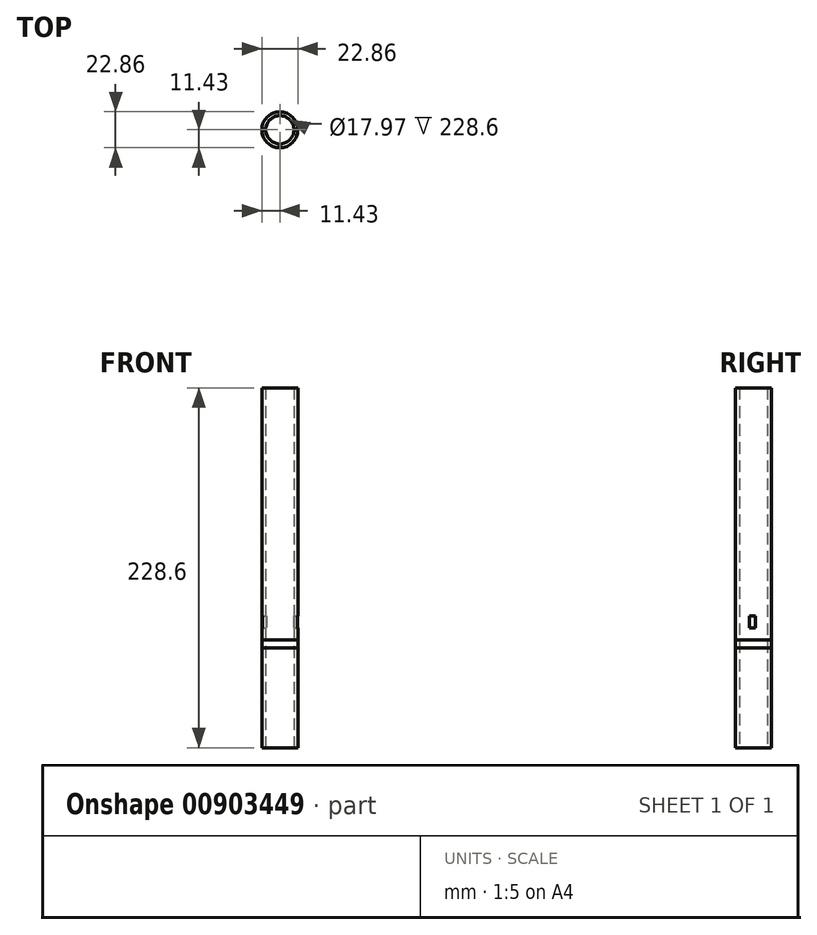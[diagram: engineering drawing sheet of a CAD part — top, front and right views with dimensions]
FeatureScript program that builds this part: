
annotation { "Feature Type Name" : "Feature", "Feature Type Description" : "" }
export const myFeature = defineFeature(function(context is Context, id is Id, definition is map)
    precondition{}
    {
        {
            var Q0;
            Q0=qCreatedBy(makeId("Top.planeOp"),FACE);
            var sketch = newSketch(context, id + "F0", { "sketchPlane" : qUnion([Q0])});
            skCircle(sketch, "E0", {"center": v(0, 0) * mm, "radius": 8.99 * mm});
            skCircle(sketch, "E1", {"center": v(0, 0) * mm, "radius": 11.43 * mm});
            skSolve(sketch);
        }
        {
            var Q0;
            Q0=makeQuery(id+"F0.imprint","IMPRINT",FACE,{"disambiguationData":[TD([[makeQuery(id+"F0.imprint","IMPRINT",EDGE,{"derivedFrom":sQuery(id+"F0.wireOp",EDGE,"E0")}),-1.0]])]});
            extrude(context, id + "F1", {"entities" : qUnion([Q0]), "depth" : 228.6 * mm, "offsetDistance" : 25.4 * mm});
        }
        {
            var Q0;
            Q0=qCreatedBy(makeId("Top.planeOp"),FACE);
            cPlane(context, id + "F2", {"entities" : qUnion([Q0]), "cplaneType" : CPlaneType.OFFSET, "offset" : 76.2 * mm, "width" : 152.4 * mm, "height" : 152.4 * mm});
        }
        {
            var Q0;
            Q0=qCreatedBy(id+"F2.planeOp",FACE);
            var sketch = newSketch(context, id + "F3", { "sketchPlane" : qUnion([Q0])});
            skLineSegment(sketch, "E2.bottom", {"start": v(-13.95, 1.1) * mm, "end": v(14.76, 1.1) * mm});
            skLineSegment(sketch, "E2.top", {"start": v(-13.95, -2.74) * mm, "end": v(14.76, -2.74) * mm});
            skLineSegment(sketch, "E2.left", {"start": v(-13.95, 1.1) * mm, "end": v(-13.95, -2.74) * mm});
            skLineSegment(sketch, "E2.right", {"start": v(14.76, 1.1) * mm, "end": v(14.76, -2.74) * mm});
            skSolve(sketch);
        }
        {
            var Q0;
            Q0=makeQuery(id+"F3.imprint","IMPRINT",FACE,{"disambiguationData":[TD([[makeQuery(id+"F3.imprint","IMPRINT",EDGE,{"derivedFrom":sQuery(id+"F3.wireOp",EDGE,"E2.bottom")}),-1.0]])]});
            extrude(context, id + "F4", {"entities" : qUnion([Q0]), "operationType" : NewBodyOperationType.REMOVE, "depth" : 7.62 * mm, "offsetDistance" : 25.4 * mm});
        }
        {
            var Q0;
            Q0=qCreatedBy(makeId("Top.planeOp"),FACE);
            cPlane(context, id + "F5", {"entities" : qUnion([Q0]), "cplaneType" : CPlaneType.OFFSET, "offset" : 63.5 * mm, "width" : 152.4 * mm, "height" : 152.4 * mm});
        }
        {
            var Q0;
            Q0=qCreatedBy(id+"F5.planeOp",FACE);
            var sketch = newSketch(context, id + "F6", { "sketchPlane" : qUnion([Q0])});
            skCircle(sketch, "E3", {"center": v(0, 0) * mm, "radius": 11.43 * mm});
            skSolve(sketch);
        }
        {
            var Q0;
            Q0=makeQuery(id+"F6.imprint","IMPRINT",FACE,{"disambiguationData":[TD([[makeQuery(id+"F6.imprint","IMPRINT",EDGE,{"derivedFrom":sQuery(id+"F6.wireOp",EDGE,"E3")}),1.0]])]});
            extrude(context, id + "F7", {"entities" : qUnion([Q0]), "depth" : 5.08 * mm, "offsetDistance" : 25.4 * mm});
        }
    });
